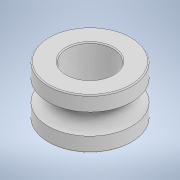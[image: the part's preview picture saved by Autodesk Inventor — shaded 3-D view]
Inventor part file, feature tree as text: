
AUTODESK INVENTOR PART (.ipt)
format: ipt  version: 2021 (Build 250183000, 183)  size: 178,176 bytes
history: native  units: in
note: dims shown in document units (in); Inventor stores cm internally (conversion verified against a paired STEP export)
features: revolve x1, mirror x1, fillet x1, sketch x1
ambient origin geometry x8: Origin, YZ Plane, XZ Plane, XY Plane, X Axis, Y Axis, Z Axis, Center Point
bodies: Solid1 (feature_tree)
feature tree (4):
  revolve  "Revolution1"  [1 undecoded]
  mirror  "Mirror1"
  fillet  "Fillet1"  Radius=0.4331in
  sketch  "Sketch1"  dims[d0=0.7874in d1=0.4724in d2=0.4331in d3=0.0in d4=0.1969in d5=90.0deg d6=0.0197in]
note: 1 required parameter value undecoded (feature->parameter linkage not recoverable at this tier; creation-order binding heuristic only, values carry confidence <= 0.55)
